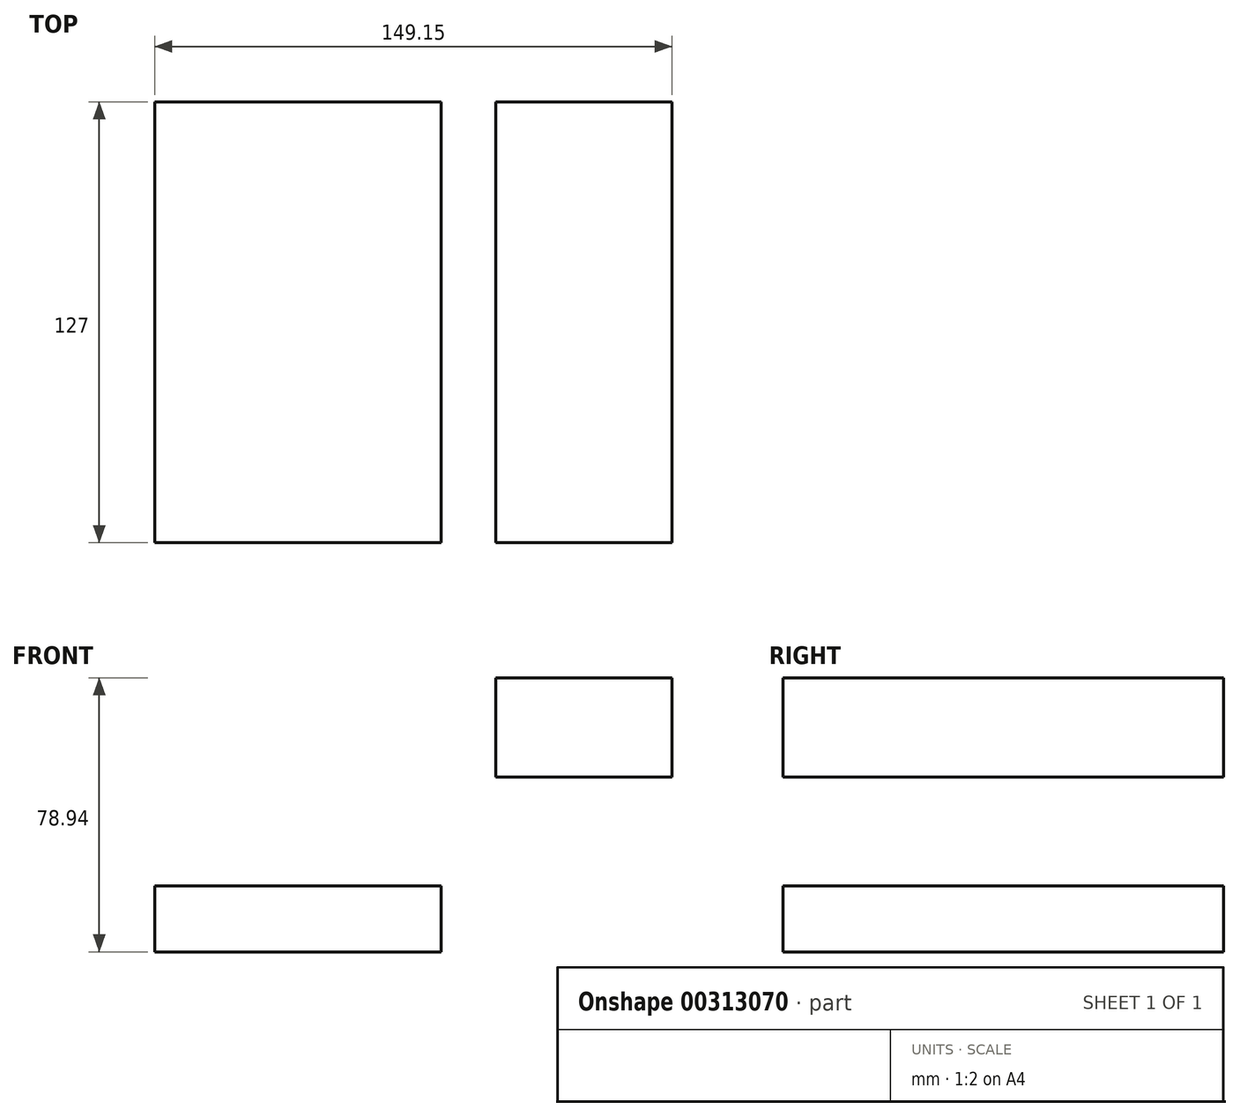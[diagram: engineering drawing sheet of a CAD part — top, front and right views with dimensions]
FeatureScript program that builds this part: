
annotation { "Feature Type Name" : "Feature", "Feature Type Description" : "" }
export const myFeature = defineFeature(function(context is Context, id is Id, definition is map)
    precondition{}
    {
        {
            var Q0;
            Q0=qCreatedBy(makeId("Front.planeOp"),FACE);
            var sketch = newSketch(context, id + "F0", { "sketchPlane" : qUnion([Q0])});
            skLineSegment(sketch, "E0.bottom", {"start": v(-41.28, 9.52) * mm, "end": v(41.27, 9.53) * mm});
            skLineSegment(sketch, "E0.top", {"start": v(-41.28, -9.53) * mm, "end": v(41.28, -9.53) * mm});
            skLineSegment(sketch, "E0.left", {"start": v(-41.28, 9.52) * mm, "end": v(-41.28, -9.53) * mm});
            skLineSegment(sketch, "E0.right", {"start": v(41.27, 9.53) * mm, "end": v(41.28, -9.52) * mm});
            skPoint(sketch, "E0.middle", {"position": v(0, 0) * mm});
            skLineSegment(sketch, "E1.bottom", {"start": v(57.08, 40.84) * mm, "end": v(107.88, 40.84) * mm});
            skLineSegment(sketch, "E1.top", {"start": v(57.08, 69.41) * mm, "end": v(107.88, 69.41) * mm});
            skLineSegment(sketch, "E1.left", {"start": v(57.08, 40.84) * mm, "end": v(57.08, 69.41) * mm});
            skLineSegment(sketch, "E1.right", {"start": v(107.88, 40.84) * mm, "end": v(107.88, 69.41) * mm});
            skPoint(sketch, "E1.middle", {"position": v(82.48, 55.12) * mm});
            skLineSegment(sketch, "E2", {"start": v(41.27, 9.53) * mm, "end": v(41.27, 46.97) * mm});
            skArc(sketch, "E3", {"start": v(41.27, 46.97) * mm, "mid": v(45.92, 58.2) * mm, "end": v(57.15, 62.85) * mm});
            skLineSegment(sketch, "E4", {"start": v(57.15, 62.85) * mm, "end": v(82.48, 62.85) * mm});
            skPoint(sketch, "E4.endSnap0", {"position": v(82.48, 40.84) * mm});
            skLineSegment(sketch, "E5", {"start": v(82.48, 62.85) * mm, "end": v(79.14, 62.85) * mm});
            skSolve(sketch);
        }
        {
            var Q0;
            Q0 = qSketchRegion(id + "F0", true);
            extrude(context, id + "F1", {"entities" : qUnion([Q0]), "endBound" : BoundingType.SYMMETRIC, "depth" : 127 * mm});
        }
    });
